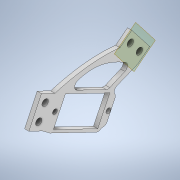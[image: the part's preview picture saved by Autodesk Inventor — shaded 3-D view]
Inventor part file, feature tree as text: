
AUTODESK INVENTOR PART (.ipt)
format: ipt  version: 2020 (Build 240168000, 168)  size: 264,192 bytes
history: native  units: mm
features: other x5, extrude x4, sketch x3, projected_geometry x3, fillet x2, reference x2, plane x1
ambient origin geometry x8: Origin, YZ Plane, XZ Plane, XY Plane, X Axis, Y Axis, Z Axis, Center Point
bodies: Solid1 (feature_tree)
feature tree (20):
  plane  "Work Plane1"
  extrude  "Extrusion1"  Depth=10.0mm TaperAngle=0.0deg
  extrude  "Extrusion2"  Depth=10.0mm TaperAngle=0.0deg
  fillet  "Fillet1"  Radius=2.0mm
  extrude  "Extrusion3"  Depth=10.0mm TaperAngle=0.0deg
  fillet  "Fillet2"  [1 undecoded]
  extrude  "Extrusion4"  [1 undecoded]
  sketch  "Sketch1"  dims[d0=2.0mm d1=0.0mm d2=10.0mm d3=0.0mm]
  reference  "Reference1"
  reference  "Reference2"
  projected_geometry  "Projected Loop1"
  sketch  "Sketch3"  dims[d4=2.0mm d5=10.0mm d6=0.0mm d7=2.0mm]
  projected_geometry  "Projected Loop2"
  sketch  "Sketch4"  dims[d8=0.4mm d9=10.0mm d10=0.0mm]
  projected_geometry  "Projected Loop3"
  other  "<userpath>\Documents\Inventor\CC_RENEV\belzebub.iam"
  other  "belzebub.iam"
  other  "Part7:1"
  other  "Part7:2"
  other  "Assembly1"
note: 2 required parameter values undecoded (feature->parameter linkage not recoverable at this tier; creation-order binding heuristic only, values carry confidence <= 0.55)
